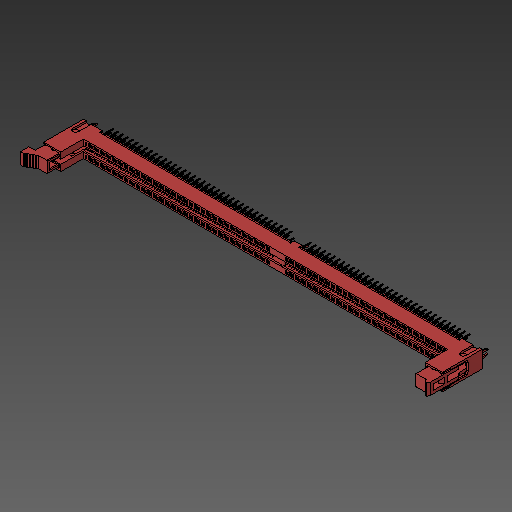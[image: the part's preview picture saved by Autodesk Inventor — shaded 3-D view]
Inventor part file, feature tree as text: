
AUTODESK INVENTOR PART (.ipt)
format: ipt  version: 2018.2 (Build 222227000, 227)  size: 4,004,864 bytes
history: native  units: mm
features: other x1, mirror x1
ambient origin geometry x8: Origin, YZ Plane, XZ Plane, XY Plane, X Axis, Y Axis, Z Axis, Center Point
bodies: Body1 (feature_tree)
feature tree (2):
  other  "ソリッド1"
  mirror  "Mirror2"
